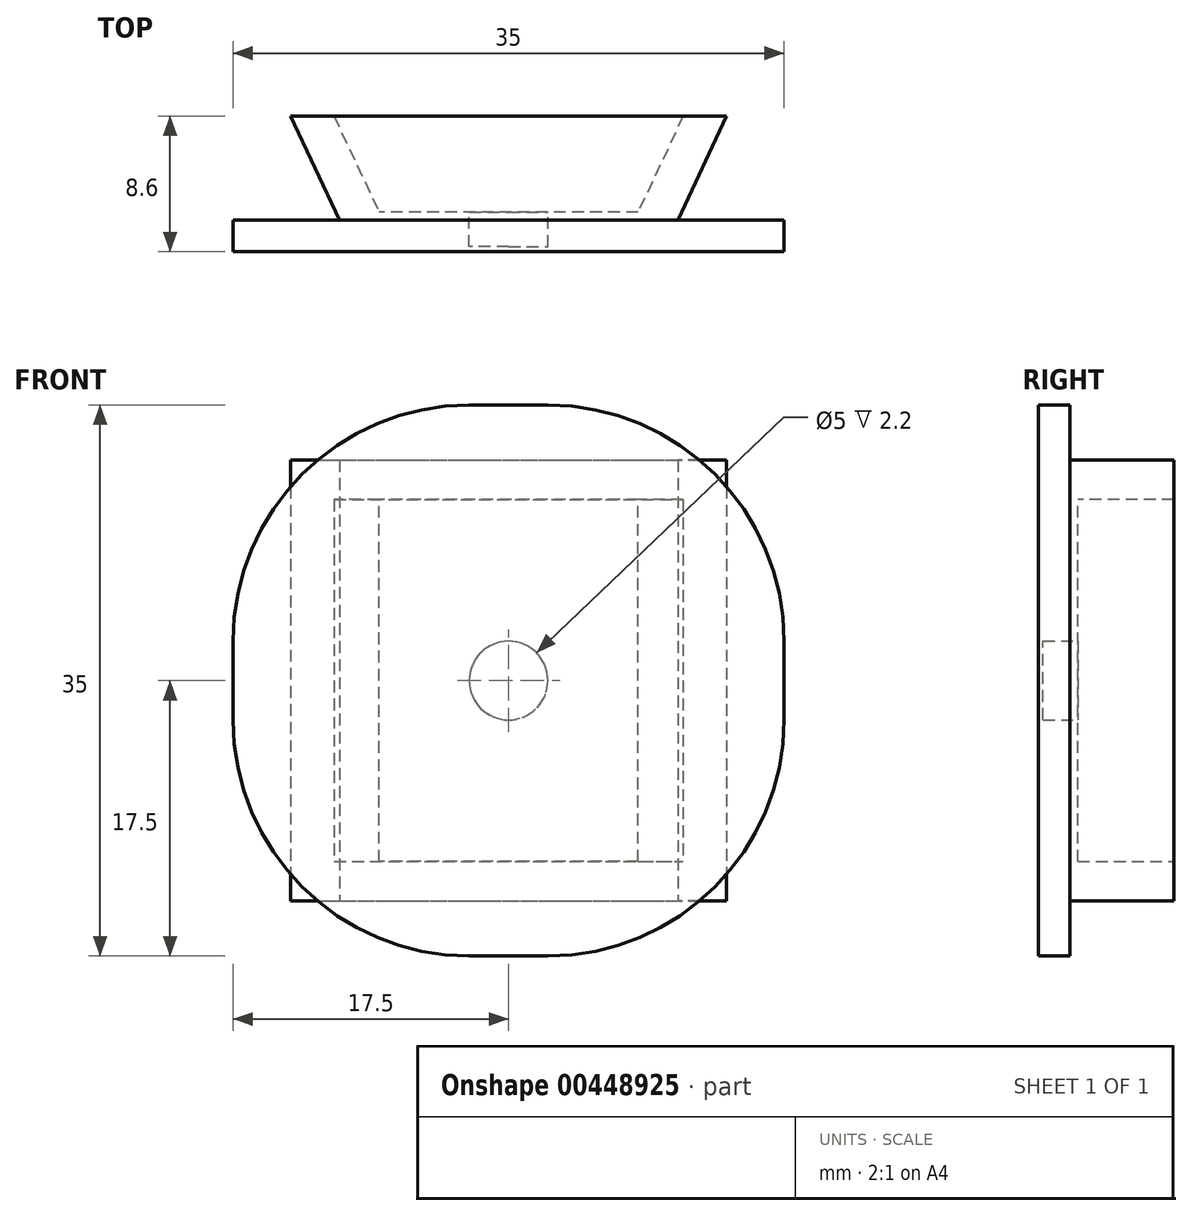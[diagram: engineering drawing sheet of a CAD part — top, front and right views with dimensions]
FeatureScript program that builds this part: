
annotation { "Feature Type Name" : "Feature", "Feature Type Description" : "" }
export const myFeature = defineFeature(function(context is Context, id is Id, definition is map)
    precondition{}
    {
        {
            var Q0;
            Q0=qCreatedBy(makeId("Top.planeOp"),FACE);
            var sketch = newSketch(context, id + "F0", { "sketchPlane" : qUnion([Q0])});
            skLineSegment(sketch, "E0.bottom", {"start": v(11, -20.55) * mm, "end": v(-11, -20.55) * mm});
            skLineSegment(sketch, "E0.top", {"start": v(11, 20.55) * mm, "end": v(-11, 20.55) * mm});
            skLineSegment(sketch, "E0.right", {"start": v(-11, -20.55) * mm, "end": v(-11, 20.55) * mm});
            skPoint(sketch, "E0.middle", {"position": v(0, 0) * mm});
            skLineSegment(sketch, "E1.0", {"start": v(11.44, -25.55) * mm, "end": v(-16, -25.55) * mm});
            skLineSegment(sketch, "E1.1", {"start": v(-16, -25.55) * mm, "end": v(-16, 25.55) * mm});
            skLineSegment(sketch, "E1.2", {"start": v(11.44, 25.55) * mm, "end": v(-16, 25.55) * mm});
            skLineSegment(sketch, "E2", {"start": v(11, 20.55) * mm, "end": v(11, 18.05) * mm});
            skLineSegment(sketch, "E3", {"start": v(11, 18.05) * mm, "end": v(20.79, 25.55) * mm});
            skLineSegment(sketch, "E4", {"start": v(20.79, 25.55) * mm, "end": v(11.44, 25.55) * mm});
            skLineSegment(sketch, "E5", {"start": v(-46.78, 0) * mm, "end": v(45.2, 0) * mm, "construction": true});
            skLineSegment(sketch, "E6.MirrorCS", {"start": v(11, -18.05) * mm, "end": v(20.79, -25.55) * mm});
            skLineSegment(sketch, "E7.MirrorCS", {"start": v(20.79, -25.55) * mm, "end": v(11.44, -25.55) * mm});
            skLineSegment(sketch, "E8.MirrorCS", {"start": v(11, -20.55) * mm, "end": v(11, -18.05) * mm});
            skLineSegment(sketch, "E9", {"start": v(16.11, 25.55) * mm, "end": v(15.9, 21.8) * mm});
            skLineSegment(sketch, "E10.MirrorCS", {"start": v(16.11, -25.55) * mm, "end": v(15.9, -21.8) * mm});
            skSolve(sketch);
        }
        {
            var Q0;
            Q0=makeQuery(id+"F0.imprint","IMPRINT",FACE,{"disambiguationData":[TD([[makeQuery(id+"F0.imprint","IMPRINT",EDGE,{"derivedFrom":sQuery(id+"F0.wireOp",EDGE,"E0.bottom")}),1.0]])]});
            extrude(context, id + "F1", {"entities" : qUnion([Q0]), "depth" : 6 * mm});
        }
        {
            var Q0;
            Q0=makeQuery(id+"F1.opExtrude","CAP_FACE",FACE,{"disambiguationData":[OSD([sQuery(id+"F0.wireOp",EDGE,"E0.bottom"),sQuery(id+"F0.wireOp",EDGE,"E0.top"),sQuery(id+"F0.wireOp",EDGE,"E0.right"),sQuery(id+"F0.wireOp",EDGE,"E1.0"),sQuery(id+"F0.wireOp",EDGE,"E1.1"),sQuery(id+"F0.wireOp",EDGE,"E1.2"),sQuery(id+"F0.wireOp",EDGE,"E2"),sQuery(id+"F0.wireOp",EDGE,"E3"),sQuery(id+"F0.wireOp",EDGE,"E4"),sQuery(id+"F0.wireOp",EDGE,"E6.MirrorCS"),sQuery(id+"F0.wireOp",EDGE,"E7.MirrorCS"),sQuery(id+"F0.wireOp",EDGE,"E8.MirrorCS")])],"isStart":true});
            var sketch = newSketch(context, id + "F2", { "sketchPlane" : qUnion([Q0])});
            skLineSegment(sketch, "E11.bottom", {"start": v(-16, -25.55) * mm, "end": v(-11, -25.55) * mm});
            skLineSegment(sketch, "E11.top", {"start": v(-16, -40.55) * mm, "end": v(-11, -40.55) * mm});
            skLineSegment(sketch, "E11.left", {"start": v(-16, -25.55) * mm, "end": v(-16, -40.55) * mm});
            skLineSegment(sketch, "E11.right", {"start": v(-11, -25.55) * mm, "end": v(-11, -36.55) * mm});
            skLineSegment(sketch, "E12.bottom", {"start": v(-11, -40.55) * mm, "end": v(4, -40.55) * mm});
            skLineSegment(sketch, "E12.top", {"start": v(-11, -36.55) * mm, "end": v(4, -36.55) * mm});
            skLineSegment(sketch, "E12.right", {"start": v(4, -40.55) * mm, "end": v(4, -36.55) * mm});
            skSolve(sketch);
        }
        {
            var Q0;
            Q0=qSketchRegion(id+"F2",true);
            extrude(context, id + "F3", {"entities" : qUnion([Q0]), "operationType" : NewBodyOperationType.ADD, "oppositeDirection" : true, "depth" : 15 * mm});
        }
        {
            var Q0;
            Q0=makeQuery(id+"F3.opExtrude","SWEPT_FACE",FACE,{"disambiguationData":[OSD([sQuery(id+"F2.wireOp",EDGE,"E11.right")])]});
            var sketch = newSketch(context, id + "F4", { "sketchPlane" : qUnion([Q0])});
            skLineSegment(sketch, "E13", {"start": v(25.55, 6) * mm, "end": v(25.55, 15) * mm});
            skLineSegment(sketch, "E14", {"start": v(25.55, 15) * mm, "end": v(36.55, 15) * mm});
            skLineSegment(sketch, "E15", {"start": v(25.55, 6) * mm, "end": v(29.55, 6) * mm});
            skLineSegment(sketch, "E16", {"start": v(29.55, 6) * mm, "end": v(36.55, 15) * mm});
            skSolve(sketch);
        }
        {
            var Q0;
            Q0=qSketchRegion(id+"F4",true);
            var Q1;
            Q1=makeQuery(id+"F3.boolean.opBoolean","MERGE",FACE,{"derivedFrom":[makeQuery(id+"F1.opExtrude","SWEPT_FACE",FACE,{"disambiguationData":[OSD([sQuery(id+"F0.wireOp",EDGE,"E1.1")])]}),makeQuery(id+"F3.opExtrude","SWEPT_FACE",FACE,{"disambiguationData":[OSD([sQuery(id+"F2.wireOp",EDGE,"E11.left")])]})]});
            extrude(context, id + "F5", {"entities" : qUnion([Q0]), "operationType" : NewBodyOperationType.REMOVE, "endBound" : BoundingType.UP_TO_SURFACE, "oppositeDirection" : true, "endBoundEntityFace" : qUnion([Q1]), "depth" : 25 * mm});
        }
        {
            var Q0;
            Q0=makeQuery(id+"F3.opExtrude","CAP_EDGE",EDGE,{"disambiguationData":[OSD([sQuery(id+"F2.wireOp",EDGE,"E12.right")])],"isStart":false});
            fillet(context, id + "F6", {"entities" : qUnion([Q0]), "radius" : 5 * mm, "tangentPropagation" : true, "allowEdgeOverflow" : false});
        }
        {
            var Q0;
            Q0=makeQuery(id+"F3.opExtrude","SWEPT_FACE",FACE,{"disambiguationData":[OSD([sQuery(id+"F2.wireOp",EDGE,"E11.top"),sQuery(id+"F2.wireOp",EDGE,"E12.bottom")])]});
            cPlane(context, id + "F7", {"entities" : qUnion([Q0]), "cplaneType" : CPlaneType.OFFSET, "offset" : 25 * mm, "width" : 150 * mm, "height" : 150 * mm});
        }
        {
            var Q0;
            Q0=makeQuery(id+"F3.opExtrude","SWEPT_FACE",FACE,{"disambiguationData":[OSD([sQuery(id+"F2.wireOp",EDGE,"E11.top"),sQuery(id+"F2.wireOp",EDGE,"E12.bottom")])]});
            cPlane(context, id + "F8", {"entities" : qUnion([Q0]), "cplaneType" : CPlaneType.OFFSET, "offset" : 48 * mm, "width" : 150 * mm, "height" : 150 * mm});
        }
        {
            var Q0;
            Q0=qCreatedBy(id+"F7.planeOp",FACE);
            var sketch = newSketch(context, id + "F9", { "sketchPlane" : qUnion([Q0])});
            skLineSegment(sketch, "E17.0.0", {"start": v(16, 15) * mm, "end": v(1, 15) * mm});
            skArc(sketch, "E17.0.1", {"start": v(1, 15) * mm, "mid": v(-2.54, 13.54) * mm, "end": v(-4, 10) * mm});
            skLineSegment(sketch, "E17.0.2", {"start": v(-4, 10) * mm, "end": v(-4, 0) * mm});
            skLineSegment(sketch, "E17.0.3", {"start": v(-4, 0) * mm, "end": v(16, 0) * mm});
            skLineSegment(sketch, "E17.0.4", {"start": v(16, 0) * mm, "end": v(16, 15) * mm});
            skSolve(sketch);
        }
        {
            var Q0;
            Q0=makeQuery(id+"F9.imprint","IMPRINT",FACE,{"disambiguationData":[TD([[makeQuery(id+"F9.imprint","IMPRINT",EDGE,{"derivedFrom":sQuery(id+"F9.wireOp",EDGE,"E17.0.0")}),1.0]])]});
            extrude(context, id + "F10", {"entities" : qUnion([Q0]), "depth" : 5 * mm});
        }
        {
            var Q0;
            Q0=qCreatedBy(id+"F8.planeOp",FACE);
            var sketch = newSketch(context, id + "F11", { "sketchPlane" : qUnion([Q0])});
            skLineSegment(sketch, "E18.bottom", {"start": v(23.5, -10) * mm, "end": v(-11.5, -10) * mm});
            skLineSegment(sketch, "E18.top", {"start": v(23.5, 25) * mm, "end": v(-11.5, 25) * mm});
            skLineSegment(sketch, "E18.left", {"start": v(23.5, -10) * mm, "end": v(23.5, 25) * mm});
            skLineSegment(sketch, "E18.right", {"start": v(-11.5, -10) * mm, "end": v(-11.5, 25) * mm});
            skPoint(sketch, "E18.middle", {"position": v(6, 7.5) * mm});
            skPoint(sketch, "E18.middle.positionSnap0", {"position": v(16, 7.5) * mm});
            skPoint(sketch, "E18.middle.positionSnap1", {"position": v(6, 0) * mm});
            skPoint(sketch, "E18.centerSnap0", {"position": v(16, 7.5) * mm});
            skPoint(sketch, "E18.centerSnap1", {"position": v(6, 0) * mm});
            skSolve(sketch);
        }
        {
            var Q0;
            Q0=qSketchRegion(id+"F11",true);
            extrude(context, id + "F12", {"entities" : qUnion([Q0]), "operationType" : NewBodyOperationType.ADD, "depth" : 2 * mm});
        }
        {
            var Q0;
            Q0=makeQuery(id+"F12.opExtrude","CAP_FACE",FACE,{"disambiguationData":[OSD([sQuery(id+"F11.wireOp",EDGE,"E18.bottom"),sQuery(id+"F11.wireOp",EDGE,"E18.top"),sQuery(id+"F11.wireOp",EDGE,"E18.left"),sQuery(id+"F11.wireOp",EDGE,"E18.right")])],"isStart":false});
            var sketch = newSketch(context, id + "F13", { "sketchPlane" : qUnion([Q0])});
            skLineSegment(sketch, "E19.bottom", {"start": v(16.75, 21.5) * mm, "end": v(-4.75, 21.5) * mm});
            skLineSegment(sketch, "E19.top", {"start": v(16.75, -6.5) * mm, "end": v(-4.75, -6.5) * mm});
            skLineSegment(sketch, "E19.left", {"start": v(16.75, 21.5) * mm, "end": v(16.75, -6.5) * mm});
            skLineSegment(sketch, "E19.right", {"start": v(-4.75, 21.5) * mm, "end": v(-4.75, -6.5) * mm});
            skPoint(sketch, "E19.middle", {"position": v(6, 7.5) * mm});
            skPoint(sketch, "E19.middle.positionSnap0", {"position": v(-11.5, 7.5) * mm});
            skPoint(sketch, "E19.middle.positionSnap1", {"position": v(6, 25) * mm});
            skPoint(sketch, "E19.centerSnap0", {"position": v(-11.5, 7.5) * mm});
            skPoint(sketch, "E19.centerSnap1", {"position": v(6, 25) * mm});
            skSolve(sketch);
        }
        {
            var Q0;
            Q0=makeQuery(id+"F13.imprint","IMPRINT",FACE,{"disambiguationData":[TD([[makeQuery(id+"F13.imprint","IMPRINT",EDGE,{"derivedFrom":sQuery(id+"F13.wireOp",EDGE,"E19.bottom")}),1.0]])]});
            cPlane(context, id + "F14", {"entities" : qUnion([Q0]), "cplaneType" : CPlaneType.OFFSET, "offset" : 6.6 * mm, "width" : 150 * mm, "height" : 150 * mm});
        }
        {
            var Q0;
            Q0=qCreatedBy(id+"F14.planeOp",FACE);
            var sketch = newSketch(context, id + "F15", { "sketchPlane" : qUnion([Q0])});
            skLineSegment(sketch, "E20.0.0", {"start": v(-4.75, -6.5) * mm, "end": v(16.75, -6.5) * mm, "construction": true});
            skLineSegment(sketch, "E20.0.1", {"start": v(16.75, -6.5) * mm, "end": v(16.75, 21.5) * mm, "construction": true});
            skLineSegment(sketch, "E20.0.2", {"start": v(16.75, 21.5) * mm, "end": v(-4.75, 21.5) * mm, "construction": true});
            skLineSegment(sketch, "E20.0.3", {"start": v(-4.75, 21.5) * mm, "end": v(-4.75, -6.5) * mm, "construction": true});
            skLineSegment(sketch, "E21.bottom", {"start": v(19.85, 21.5) * mm, "end": v(-7.85, 21.5) * mm});
            skLineSegment(sketch, "E21.top", {"start": v(19.85, -6.5) * mm, "end": v(-7.85, -6.5) * mm});
            skLineSegment(sketch, "E21.left", {"start": v(19.85, 21.5) * mm, "end": v(19.85, -6.5) * mm});
            skLineSegment(sketch, "E21.right", {"start": v(-7.85, 21.5) * mm, "end": v(-7.85, -6.5) * mm});
            skPoint(sketch, "E21.middle", {"position": v(6, 7.5) * mm});
            skPoint(sketch, "E21.middle.positionSnap0", {"position": v(6, 21.5) * mm});
            skPoint(sketch, "E21.middle.positionSnap1", {"position": v(-4.75, 7.5) * mm});
            skPoint(sketch, "E21.centerSnap0", {"position": v(6, 21.5) * mm});
            skPoint(sketch, "E21.centerSnap1", {"position": v(-4.75, 7.5) * mm});
            skSolve(sketch);
        }
        {
            var Q2;
            Q2=makeQuery(id+"F15.imprint","IMPRINT",FACE,{"disambiguationData":[TD([[makeQuery(id+"F15.imprint","IMPRINT",EDGE,{"derivedFrom":sQuery(id+"F15.wireOp",EDGE,"E21.bottom")}),1.0]])]});
            var Q3;
            Q3=makeQuery(id+"F13.imprint","IMPRINT",FACE,{"disambiguationData":[TD([[makeQuery(id+"F13.imprint","IMPRINT",EDGE,{"derivedFrom":sQuery(id+"F13.wireOp",EDGE,"E19.bottom")}),1.0]])]});
            loft(context, id + "F16", {"operationType" : NewBodyOperationType.ADD, "sheetProfilesArray" : [{ "sheetProfileEntities" : qUnion([Q2]) }, { "sheetProfileEntities" : qUnion([Q3]) }]});
        }
        {
            var Q0;
            Q0=makeQuery(id+"F16.opLoft","CAP_FACE",FACE,{"disambiguationData":[OSD([makeQuery(id+"F15.imprint","IMPRINT",FACE,{"disambiguationData":[TD([[makeQuery(id+"F15.imprint","IMPRINT",EDGE,{"derivedFrom":sQuery(id+"F15.wireOp",EDGE,"E21.bottom")}),1.0]])]})])],"isStart":true});
            shell(context, id + "F17", {"entities" : qUnion([Q0]), "thickness" : 2.5 * mm});
        }
        {
            var Q0;
            Q0=makeQuery(id+"F10.opExtrude","SWEPT_BODY",BODY,{"disambiguationData":[OSD([sQuery(id+"F9.wireOp",EDGE,"E17.0.0"),sQuery(id+"F9.wireOp",EDGE,"E17.0.1"),sQuery(id+"F9.wireOp",EDGE,"E17.0.2"),sQuery(id+"F9.wireOp",EDGE,"E17.0.3"),sQuery(id+"F9.wireOp",EDGE,"E17.0.4")])]});
            deleteBodies(context, id + "F18", {"entities" : qUnion([Q0])});
        }
        {
            var Q0;
            Q0=makeQuery(id+"F17.opShell","OFFSET_FACE",FACE,{"disambiguationData":[OSD([sQuery(id+"F11.wireOp",EDGE,"E18.bottom"),sQuery(id+"F11.wireOp",EDGE,"E18.top"),sQuery(id+"F11.wireOp",EDGE,"E18.left"),sQuery(id+"F11.wireOp",EDGE,"E18.right")])]});
            var sketch = newSketch(context, id + "F19", { "sketchPlane" : qUnion([Q0])});
            skLineSegment(sketch, "E22.0.0", {"start": v(14.22, 19) * mm, "end": v(-2.22, 19) * mm, "construction": true});
            skLineSegment(sketch, "E22.0.1", {"start": v(-2.22, 19) * mm, "end": v(-2.22, -4) * mm, "construction": true});
            skLineSegment(sketch, "E22.0.2", {"start": v(-2.22, -4) * mm, "end": v(14.22, -4) * mm, "construction": true});
            skLineSegment(sketch, "E22.0.3", {"start": v(14.22, -4) * mm, "end": v(14.22, 19) * mm, "construction": true});
            skCircle(sketch, "E23", {"center": v(6, 7.5) * mm, "radius": 2.5 * mm});
            skPoint(sketch, "E23.centerSnap0", {"position": v(14.22, 7.5) * mm});
            skPoint(sketch, "E23.centerSnap1", {"position": v(6, 19) * mm});
            skSolve(sketch);
        }
        {
            var Q0;
            Q0=qSketchRegion(id+"F19",true);
            var Q1;
            Q1=makeQuery(id+"F3.opExtrude","SWEPT_FACE",FACE,{"disambiguationData":[OSD([sQuery(id+"F2.wireOp",EDGE,"E12.top")])]});
            extrude(context, id + "F20", {"entities" : qUnion([Q0]), "operationType" : NewBodyOperationType.REMOVE, "endBound" : BoundingType.UP_TO_SURFACE, "oppositeDirection" : true, "endBoundEntityFace" : qUnion([Q1]), "depth" : 100 * mm});
        }
        {
            var Q0;
            Q0=makeQuery(id+"F12.opExtrude","SWEPT_EDGE",EDGE,{"disambiguationData":[OSD([sQuery(id+"F11.wireOp",EDGE,"E18.top"),sQuery(id+"F11.wireOp",EDGE,"E18.right")])]});
            var Q1;
            Q1=makeQuery(id+"F12.opExtrude","SWEPT_EDGE",EDGE,{"disambiguationData":[OSD([sQuery(id+"F11.wireOp",EDGE,"E18.top"),sQuery(id+"F11.wireOp",EDGE,"E18.left")])]});
            var Q2;
            Q2=makeQuery(id+"F12.opExtrude","SWEPT_EDGE",EDGE,{"disambiguationData":[OSD([sQuery(id+"F11.wireOp",EDGE,"E18.bottom"),sQuery(id+"F11.wireOp",EDGE,"E18.left")])]});
            var Q3;
            Q3=makeQuery(id+"F12.opExtrude","SWEPT_EDGE",EDGE,{"disambiguationData":[OSD([sQuery(id+"F11.wireOp",EDGE,"E18.bottom"),sQuery(id+"F11.wireOp",EDGE,"E18.right")])]});
            fillet(context, id + "F21", {"entities" : qUnion([Q0, Q1, Q2, Q3]), "radius" : 15 * mm, "tangentPropagation" : true, "allowEdgeOverflow" : false});
        }
        {
            var Q0;
            Q0=makeQuery(id+"F1.opExtrude","SWEPT_EDGE",EDGE,{"disambiguationData":[OSD([sQuery(id+"F0.wireOp",EDGE,"E1.0"),sQuery(id+"F0.wireOp",EDGE,"E1.1")])]});
            var Q1;
            {var subQ0=sQuery(id+"F0.wireOp",EDGE,"E4");var subQ1=sQuery(id+"F0.wireOp",EDGE,"E1.2");var subQ2=sQuery(id+"F2.wireOp",EDGE,"E11.right");Q1=makeQuery(id+"F3.boolean.opBoolean","SPLIT",EDGE,{"disambiguationData":[topologyDisambiguationEdgeConnected([makeQuery(id+"F1.opExtrude","SWEPT_FACE",FACE,{"disambiguationData":[OSD([subQ1,subQ0])]})])],"derivedFrom":makeQuery(id+"F3.opExtrude","SWEPT_EDGE",EDGE,{"disambiguationData":[OSD([subQ1,subQ0,sQuery(id+"F2.wireOp",EDGE,"E11.bottom"),subQ2])]})});}
            fillet(context, id + "F22", {"entities" : qUnion([Q0, Q1]), "radius" : 3 * mm, "tangentPropagation" : true, "allowEdgeOverflow" : false});
        }
        {
            var Q0;
            Q0=makeQuery(id+"F1.opExtrude","SWEPT_EDGE",EDGE,{"disambiguationData":[OSD([sQuery(id+"F0.wireOp",EDGE,"E3"),sQuery(id+"F0.wireOp",EDGE,"E4")])]});
            var Q1;
            Q1=makeQuery(id+"F1.opExtrude","SWEPT_EDGE",EDGE,{"disambiguationData":[OSD([sQuery(id+"F0.wireOp",EDGE,"E6.MirrorCS"),sQuery(id+"F0.wireOp",EDGE,"E7.MirrorCS")])]});
            var Q2;
            Q2=makeQuery(id+"F1.opExtrude","SWEPT_EDGE",EDGE,{"disambiguationData":[OSD([sQuery(id+"F0.wireOp",EDGE,"E6.MirrorCS"),sQuery(id+"F0.wireOp",EDGE,"E8.MirrorCS")])]});
            var Q3;
            Q3=makeQuery(id+"F1.opExtrude","SWEPT_EDGE",EDGE,{"disambiguationData":[OSD([sQuery(id+"F0.wireOp",EDGE,"E2"),sQuery(id+"F0.wireOp",EDGE,"E3")])]});
            var Q4;
            Q4=makeQuery(id+"F1.opExtrude","SWEPT_EDGE",EDGE,{"disambiguationData":[OSD([sQuery(id+"F0.wireOp",EDGE,"E0.top"),sQuery(id+"F0.wireOp",EDGE,"E0.right")])]});
            var Q5;
            Q5=makeQuery(id+"F1.opExtrude","SWEPT_EDGE",EDGE,{"disambiguationData":[OSD([sQuery(id+"F0.wireOp",EDGE,"E0.bottom"),sQuery(id+"F0.wireOp",EDGE,"E0.right")])]});
            fillet(context, id + "F23", {"entities" : qUnion([Q0, Q1, Q2, Q3, Q4, Q5]), "radius" : .5 * mm, "tangentPropagation" : true, "allowEdgeOverflow" : false});
        }
        {
            var Q0;
            Q0=makeQuery(id+"F3.opExtrude","SWEPT_EDGE",EDGE,{"disambiguationData":[OSD([sQuery(id+"F2.wireOp",EDGE,"E11.top"),sQuery(id+"F2.wireOp",EDGE,"E11.left")])]});
            var Q1;
            Q1=makeQuery(id+"F3.opExtrude","SWEPT_EDGE",EDGE,{"disambiguationData":[OSD([sQuery(id+"F2.wireOp",EDGE,"E11.right"),sQuery(id+"F2.wireOp",EDGE,"E12.top")])]});
            fillet(context, id + "F24", {"entities" : qUnion([Q0, Q1]), "radius" : 2 * mm, "tangentPropagation" : true, "allowEdgeOverflow" : false});
        }
        {
            var Q0;
            Q0=makeQuery(id+"F5.boolean.opBoolean","COPY",EDGE,{"derivedFrom":makeQuery(id+"F5.opExtrude","SWEPT_EDGE",EDGE,{"disambiguationData":[OSD([sQuery(id+"F4.wireOp",EDGE,"E15"),sQuery(id+"F4.wireOp",EDGE,"E16")])]})});
            fillet(context, id + "F25", {"entities" : qUnion([Q0]), "radius" : 6 * mm, "tangentPropagation" : true, "allowEdgeOverflow" : false});
        }
        {
            var Q0;
            Q0=makeQuery(id+"F1.opExtrude","SWEPT_BODY",BODY,{"disambiguationData":[OSD([sQuery(id+"F0.wireOp",EDGE,"E0.bottom"),sQuery(id+"F0.wireOp",EDGE,"E0.top"),sQuery(id+"F0.wireOp",EDGE,"E0.right"),sQuery(id+"F0.wireOp",EDGE,"E1.0"),sQuery(id+"F0.wireOp",EDGE,"E1.1"),sQuery(id+"F0.wireOp",EDGE,"E1.2"),sQuery(id+"F0.wireOp",EDGE,"E2"),sQuery(id+"F0.wireOp",EDGE,"E3"),sQuery(id+"F0.wireOp",EDGE,"E4"),sQuery(id+"F0.wireOp",EDGE,"E6.MirrorCS"),sQuery(id+"F0.wireOp",EDGE,"E7.MirrorCS"),sQuery(id+"F0.wireOp",EDGE,"E8.MirrorCS"),sQuery(id+"F0.wireOp",EDGE,"E9"),sQuery(id+"F0.wireOp",EDGE,"E10.MirrorCS")])]});
            deleteBodies(context, id + "F26", {"entities" : qUnion([Q0])});
        }
        {
            var Q0;
            Q0=makeQuery(id+"F12.opExtrude","CAP_FACE",FACE,{"disambiguationData":[OSD([sQuery(id+"F11.wireOp",EDGE,"E18.bottom"),sQuery(id+"F11.wireOp",EDGE,"E18.top"),sQuery(id+"F11.wireOp",EDGE,"E18.left"),sQuery(id+"F11.wireOp",EDGE,"E18.right")])],"isStart":true});
            var sketch = newSketch(context, id + "F27", { "sketchPlane" : qUnion([Q0])});
            skLineSegment(sketch, "E24.0.0", {"start": v(-3.5, 25) * mm, "end": v(-8.5, 25) * mm});
            skArc(sketch, "E24.0.1", {"start": v(-8.5, 25) * mm, "mid": v(-19.1, 20.6) * mm, "end": v(-23.5, 10) * mm});
            skLineSegment(sketch, "E24.0.2", {"start": v(-23.5, 10) * mm, "end": v(-23.5, 5) * mm});
            skArc(sketch, "E24.0.3", {"start": v(-23.5, 5) * mm, "mid": v(-19.1, -5.6) * mm, "end": v(-8.5, -10) * mm});
            skLineSegment(sketch, "E24.0.4", {"start": v(-8.5, -10) * mm, "end": v(-3.5, -10) * mm});
            skArc(sketch, "E24.0.5", {"start": v(-3.5, -10) * mm, "mid": v(7.1, -5.6) * mm, "end": v(11.5, 5) * mm});
            skLineSegment(sketch, "E24.0.6", {"start": v(11.5, 5) * mm, "end": v(11.5, 10) * mm});
            skArc(sketch, "E24.0.7", {"start": v(11.5, 10) * mm, "mid": v(7.1, 20.6) * mm, "end": v(-3.5, 25) * mm});
            skSolve(sketch);
        }
        {
            var Q0;
            Q0 = qSketchRegion(id + "F27", true);
            extrude(context, id + "F28", {"entities" : qUnion([Q0]), "operationType" : NewBodyOperationType.ADD, "oppositeDirection" : true, "depth" : .3 * mm, "offsetDistance" : 25 * mm});
        }
    });
